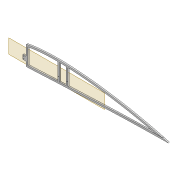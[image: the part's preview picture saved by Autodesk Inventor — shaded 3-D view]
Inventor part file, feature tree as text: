
AUTODESK INVENTOR PART (.ipt)
format: ipt  version: 2022 (Build 260153000, 153)  size: 419,328 bytes
history: native  units: mm
features: extrude x8, sketch x7, projected_geometry x6, fillet x2, shell x1, plane x1
ambient origin geometry x8: Origin, YZ Plane, XZ Plane, XY Plane, X Axis, Y Axis, Z Axis, Center Point
bodies: Solid1 (feature_tree)
feature tree (25):
  extrude  "Extrusion1"  Depth=5.0mm
  shell  "Shell1"  Thickness=2.0mm
  extrude  "Extrusion8"  Depth=5.9mm
  extrude  "Extrusion3"  Depth=10.0mm TaperAngle=0.0deg
  extrude  "Extrusion4"  Depth=2.0mm
  fillet  "Fillet1"  Radius=5.0mm
  sketch  "Sketch10"  dims[d22=4.0mm d23=0.0mm d31=2.0mm d32=5.0mm]
  extrude  "Extrusion5"  Depth=2.5mm
  plane  "Work Plane2"
  extrude  "Extrusion9"  Depth=1.6mm
  fillet  "Fillet2"  Radius=2.5mm
  extrude  "Extrusion10"  Depth=0.5mm
  extrude  "Extrusion11"  Depth=0.5mm TaperAngle=0.0deg
  sketch  "Sketch3"  dims[d0=4.0mm d1=0.0mm d2=5.0mm d7=2.0mm]
  sketch  "Sketch8"  dims[d8=2.0mm d9=5.9mm]
  sketch  "Sketch9"  dims[d13=10.0mm d14=0.0mm d16=10.0mm d17=0.0mm]
  projected_geometry  "Projected Loop4"
  projected_geometry  "Projected Loop10"
  sketch  "Sketch24"  dims[d34=1.6mm d35=2.5mm]
  projected_geometry  "Projected Loop11"
  projected_geometry  "Projected Loop12"
  projected_geometry  "Projected Loop13"
  sketch  "Sketch26"  dims[d37=5.0mm d38=1.6mm d40=2.5mm]
  projected_geometry  "Projected Loop14"
  sketch  "Sketch27"  dims[d62=80.0mm d63=6.0mm d64=4.0mm d65=0.0mm d66=3.0mm d67=12.0mm d68=5.0mm d69=10.0mm d70=12.0mm d71=3.05mm d72=10.0mm d73=0.0mm d74=2.0mm d75=100.0mm d76=20.0mm d77=0.5mm d78=10.0mm d79=0.0mm d80=10.0mm d81=0.0mm]
